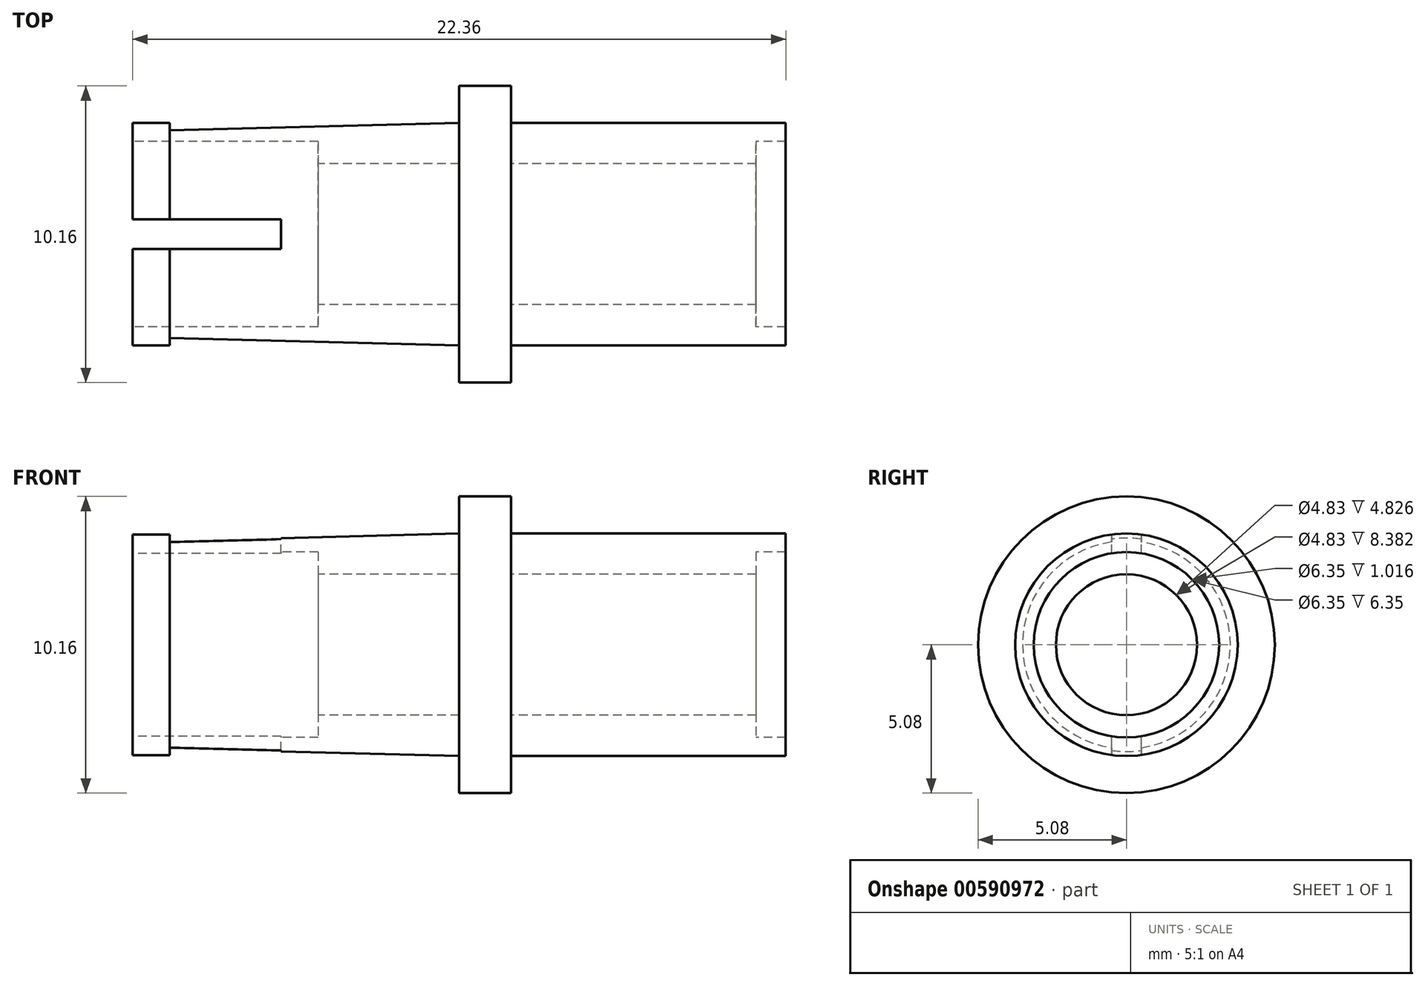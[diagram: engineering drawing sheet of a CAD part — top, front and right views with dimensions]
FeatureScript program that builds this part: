
annotation { "Feature Type Name" : "Feature", "Feature Type Description" : "" }
export const myFeature = defineFeature(function(context is Context, id is Id, definition is map)
    precondition{}
    {
        {
            var Q0;
            Q0=qCreatedBy(makeId("Front.planeOp"),FACE);
            var sketch = newSketch(context, id + "F0", { "sketchPlane" : qUnion([Q0])});
            skLineSegment(sketch, "E0", {"start": v(0, 0) * mm, "end": v(0, 2.41) * mm});
            skLineSegment(sketch, "E1", {"start": v(0, 2.41) * mm, "end": v(-4.83, 2.41) * mm});
            skLineSegment(sketch, "E2", {"start": v(-4.83, 2.41) * mm, "end": v(-4.83, 3.17) * mm});
            skLineSegment(sketch, "E3", {"start": v(-4.83, 3.17) * mm, "end": v(-11.18, 3.17) * mm});
            skLineSegment(sketch, "E4", {"start": v(-11.18, 3.17) * mm, "end": v(-11.18, 3.81) * mm});
            skLineSegment(sketch, "E5", {"start": v(-11.18, 3.81) * mm, "end": v(-9.9, 3.81) * mm});
            skLineSegment(sketch, "E6", {"start": v(-9.9, 3.8) * mm, "end": v(-9.9, 3.56) * mm});
            skLineSegment(sketch, "E7", {"start": v(-9.9, 3.56) * mm, "end": v(0, 3.81) * mm});
            skLineSegment(sketch, "E8", {"start": v(0, 3.81) * mm, "end": v(0, 5.08) * mm});
            skLineSegment(sketch, "E9", {"start": v(0, 5.08) * mm, "end": v(1.78, 5.08) * mm});
            skLineSegment(sketch, "E10", {"start": v(1.78, 5.08) * mm, "end": v(1.78, 3.8) * mm});
            skLineSegment(sketch, "E11", {"start": v(1.78, 3.8) * mm, "end": v(11.18, 3.81) * mm});
            skLineSegment(sketch, "E12", {"start": v(10.16, 3.18) * mm, "end": v(10.16, 2.41) * mm});
            skLineSegment(sketch, "E13", {"start": v(10.16, 2.41) * mm, "end": v(1.78, 2.41) * mm});
            skLineSegment(sketch, "E14", {"start": v(1.78, 2.41) * mm, "end": v(1.78, 0) * mm});
            skLineSegment(sketch, "E15", {"start": v(11.18, 3.81) * mm, "end": v(11.18, 3.18) * mm});
            skLineSegment(sketch, "E16", {"start": v(11.18, 3.18) * mm, "end": v(10.16, 3.18) * mm});
            skLineSegment(sketch, "E17", {"start": v(0, 0) * mm, "end": v(1.78, 0) * mm});
            skSolve(sketch);
        }
        {
            var Q0;
            Q0=makeQuery(id+"F0.imprint","IMPRINT",FACE,{"disambiguationData":[TD([[makeQuery(id+"F0.imprint","IMPRINT",EDGE,{"derivedFrom":sQuery(id+"F0.wireOp",EDGE,"E0")}),-1.0]])]});
            var Q1;
            Q1=sQuery(id+"F0.wireOp",EDGE,"E17");
            revolve(context, id + "F1", {"entities" : qUnion([Q0]), "axis" : qUnion([Q1]), "revolveType" : RevolveType.FULL});
        }
        {
            var Q0;
            Q0=qCreatedBy(makeId("Top.planeOp"),FACE);
            var sketch = newSketch(context, id + "F2", { "sketchPlane" : qUnion([Q0])});
            skLineSegment(sketch, "E18.0", {"start": v(-11.18, -3.81) * mm, "end": v(-11.18, 3.81) * mm});
            skLineSegment(sketch, "E19", {"start": v(-11.18, 0) * mm, "end": v(-6.1, 0) * mm, "construction": true});
            skLineSegment(sketch, "E20.0", {"start": v(-11.18, -0.5) * mm, "end": v(-6.1, -0.5) * mm});
            skLineSegment(sketch, "E21.0", {"start": v(-11.18, 0.5) * mm, "end": v(-6.1, 0.5) * mm});
            skLineSegment(sketch, "E22", {"start": v(-6.1, 0.5) * mm, "end": v(-6.1, -0.5) * mm});
            skSolve(sketch);
        }
        {
            var Q0;
            Q0 = qSketchRegion(id + "F2", true);
            extrude(context, id + "F3", {"entities" : qUnion([Q0]), "operationType" : NewBodyOperationType.REMOVE, "endBound" : BoundingType.THROUGH_ALL, "oppositeDirection" : true, "depth" : 25.4 * mm, "offsetDistance" : 25.4 * mm, "hasSecondDirection" : true, "secondDirectionBound" : SecondDirectionBoundingType.THROUGH_ALL, "secondDirectionOppositeDirection" : false, "secondDirectionDepth" : 25.4 * mm});
        }
    });
